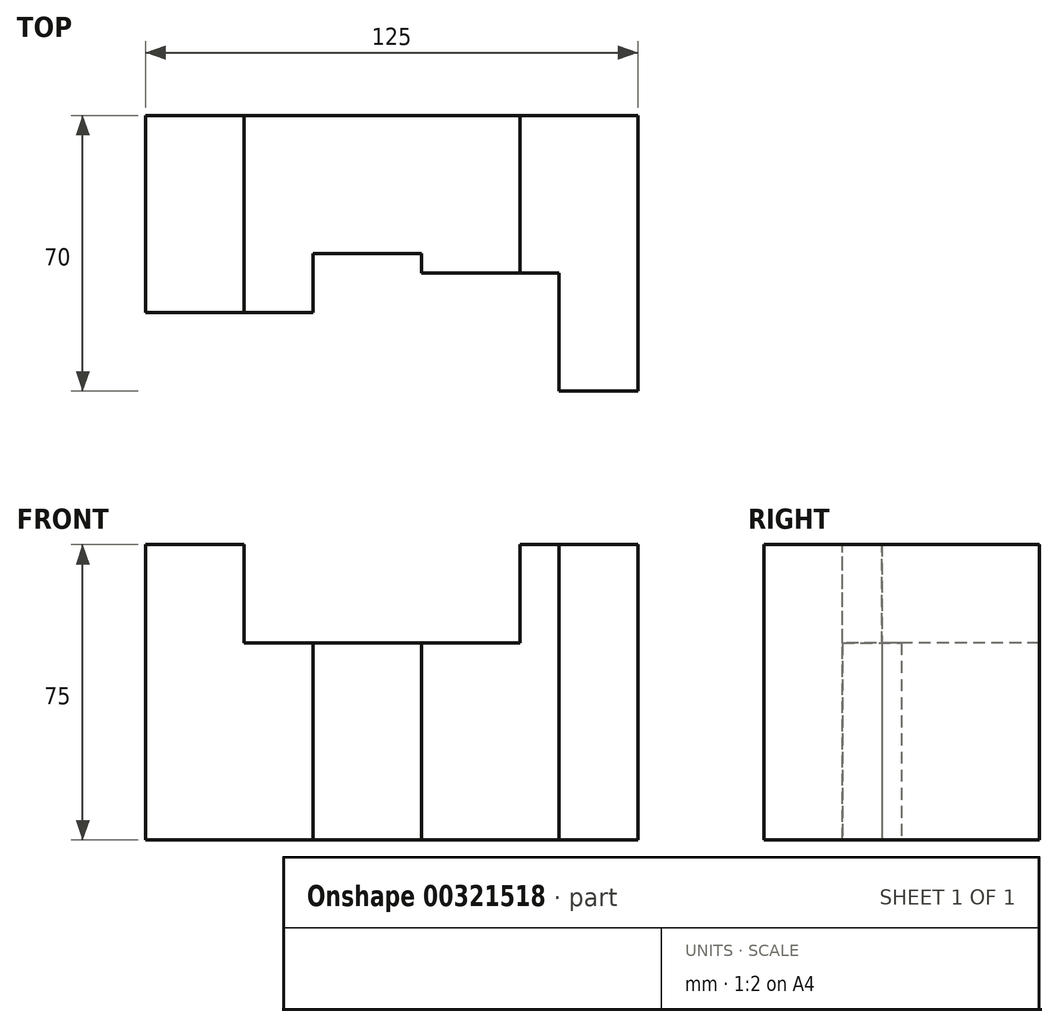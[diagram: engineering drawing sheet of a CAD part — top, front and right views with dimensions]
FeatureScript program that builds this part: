
annotation { "Feature Type Name" : "Feature", "Feature Type Description" : "" }
export const myFeature = defineFeature(function(context is Context, id is Id, definition is map)
    precondition{}
    {
        {
            var Q0;
            Q0=qCreatedBy(makeId("Front.planeOp"),FACE);
            var sketch = newSketch(context, id + "F0", { "sketchPlane" : qUnion([Q0])});
            skLineSegment(sketch, "E0.bottom", {"start": v(0, 0) * mm, "end": v(125, 0) * mm});
            skLineSegment(sketch, "E0.top", {"start": v(0, 75) * mm, "end": v(125, 75) * mm});
            skLineSegment(sketch, "E0.left", {"start": v(0, 0) * mm, "end": v(0, 75) * mm});
            skLineSegment(sketch, "E0.right", {"start": v(125, 0) * mm, "end": v(125, 75) * mm});
            skSolve(sketch);
        }
        {
            var Q0;
            Q0 = qSketchRegion(id + "F0", true);
            extrude(context, id + "F1", {"entities" : qUnion([Q0]), "depth" : (14 * 5) * mm});
        }
        {
            var Q0;
            Q0=makeQuery(id+"F1.opExtrude","CAP_FACE",FACE,{"disambiguationData":[OSD([sQuery(id+"F0.wireOp",EDGE,"E0.bottom"),sQuery(id+"F0.wireOp",EDGE,"E0.top"),sQuery(id+"F0.wireOp",EDGE,"E0.left"),sQuery(id+"F0.wireOp",EDGE,"E0.right")])],"isStart":false});
            var sketch = newSketch(context, id + "F2", { "sketchPlane" : qUnion([Q0])});
            skLineSegment(sketch, "E1.bottom", {"start": v(25, 75) * mm, "end": v(95, 75) * mm});
            skLineSegment(sketch, "E1.top", {"start": v(25, 50) * mm, "end": v(95, 50) * mm});
            skLineSegment(sketch, "E1.left", {"start": v(25, 75) * mm, "end": v(25, 50) * mm});
            skLineSegment(sketch, "E1.right", {"start": v(95, 75) * mm, "end": v(95, 50) * mm});
            skSolve(sketch);
        }
        {
            var Q0;
            Q0 = qSketchRegion(id + "F2", true);
            extrude(context, id + "F3", {"entities" : qUnion([Q0]), "operationType" : NewBodyOperationType.REMOVE, "endBound" : BoundingType.THROUGH_ALL, "oppositeDirection" : true, "depth" : 25 * mm});
        }
        {
            var Q0;
            Q0=makeQuery(id+"F1.opExtrude","CAP_FACE",FACE,{"disambiguationData":[OSD([sQuery(id+"F0.wireOp",EDGE,"E0.bottom"),sQuery(id+"F0.wireOp",EDGE,"E0.top"),sQuery(id+"F0.wireOp",EDGE,"E0.left"),sQuery(id+"F0.wireOp",EDGE,"E0.right")])],"isStart":false});
            var sketch = newSketch(context, id + "F4", { "sketchPlane" : qUnion([Q0])});
            skLineSegment(sketch, "E2.bottom", {"start": v(105, 75) * mm, "end": v(0, 75) * mm});
            skLineSegment(sketch, "E2.top", {"start": v(105, 0) * mm, "end": v(0, 0) * mm});
            skLineSegment(sketch, "E2.left", {"start": v(105, 75) * mm, "end": v(105, 0) * mm});
            skLineSegment(sketch, "E2.right", {"start": v(0, 75) * mm, "end": v(0, 0) * mm});
            skSolve(sketch);
        }
        {
            var Q0;
            Q0 = qSketchRegion(id + "F4", true);
            extrude(context, id + "F5", {"entities" : qUnion([Q0]), "operationType" : NewBodyOperationType.REMOVE, "oppositeDirection" : true, "depth" : 20 * mm});
        }
        {
            var Q0;
            Q0=makeQuery(id+"F5.boolean.opBoolean","COPY",FACE,{"derivedFrom":makeQuery(id+"F5.opExtrude","CAP_FACE",FACE,{"disambiguationData":[OSD([sQuery(id+"F4.wireOp",EDGE,"E2.bottom"),sQuery(id+"F4.wireOp",EDGE,"E2.top"),sQuery(id+"F4.wireOp",EDGE,"E2.left"),sQuery(id+"F4.wireOp",EDGE,"E2.right")])],"isStart":false})});
            var sketch = newSketch(context, id + "F6", { "sketchPlane" : qUnion([Q0])});
            skLineSegment(sketch, "E3.bottom", {"start": v(105, 75) * mm, "end": v(42.5, 75) * mm});
            skLineSegment(sketch, "E3.top", {"start": v(105, 0) * mm, "end": v(42.5, 0) * mm});
            skLineSegment(sketch, "E3.left", {"start": v(105, 75) * mm, "end": v(105, 0) * mm});
            skLineSegment(sketch, "E3.right", {"start": v(42.5, 75) * mm, "end": v(42.5, 0) * mm});
            skSolve(sketch);
        }
        {
            var Q0;
            Q0 = qSketchRegion(id + "F6", true);
            extrude(context, id + "F7", {"entities" : qUnion([Q0]), "operationType" : NewBodyOperationType.REMOVE, "oppositeDirection" : true, "depth" : 10 * mm});
        }
        {
            var Q0;
            Q0=makeQuery(id+"F7.boolean.opBoolean","COPY",FACE,{"derivedFrom":makeQuery(id+"F7.opExtrude","CAP_FACE",FACE,{"disambiguationData":[OSD([sQuery(id+"F6.wireOp",EDGE,"E3.bottom"),sQuery(id+"F6.wireOp",EDGE,"E3.top"),sQuery(id+"F6.wireOp",EDGE,"E3.left"),sQuery(id+"F6.wireOp",EDGE,"E3.right")])],"isStart":false})});
            var sketch = newSketch(context, id + "F8", { "sketchPlane" : qUnion([Q0])});
            skLineSegment(sketch, "E4.bottom", {"start": v(42.5, 50) * mm, "end": v(70, 50) * mm});
            skLineSegment(sketch, "E4.top", {"start": v(42.5, 0) * mm, "end": v(70, 0) * mm});
            skLineSegment(sketch, "E4.left", {"start": v(42.5, 50) * mm, "end": v(42.5, 0) * mm});
            skLineSegment(sketch, "E4.right", {"start": v(70, 50) * mm, "end": v(70, 0) * mm});
            skSolve(sketch);
        }
        {
            var Q0;
            Q0 = qSketchRegion(id + "F8", true);
            extrude(context, id + "F9", {"entities" : qUnion([Q0]), "operationType" : NewBodyOperationType.REMOVE, "oppositeDirection" : true, "depth" : 5 * mm});
        }
    });
